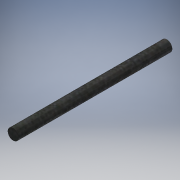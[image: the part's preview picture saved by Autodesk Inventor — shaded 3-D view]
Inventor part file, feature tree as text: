
AUTODESK INVENTOR PART (.ipt)
format: ipt  version: 2018 (Build 220112000, 112)  size: 116,224 bytes
history: native  units: mm
features: other x3, sketch x1
ambient origin geometry x8: Origin, YZ Plane, XZ Plane, XY Plane, X Axis, Y Axis, Z Axis, Center Point
bodies: Volumenkörper1 (feature_tree)
feature tree (4):
  other  "Metall Stab M5_MIR.ipt"
  other  "Volumenkörper1::Metall Stab M5_MIR.ipt"
  other  "Bezeichnung1"
  sketch  "Skizze1"  dims[d0=10.0mm]
